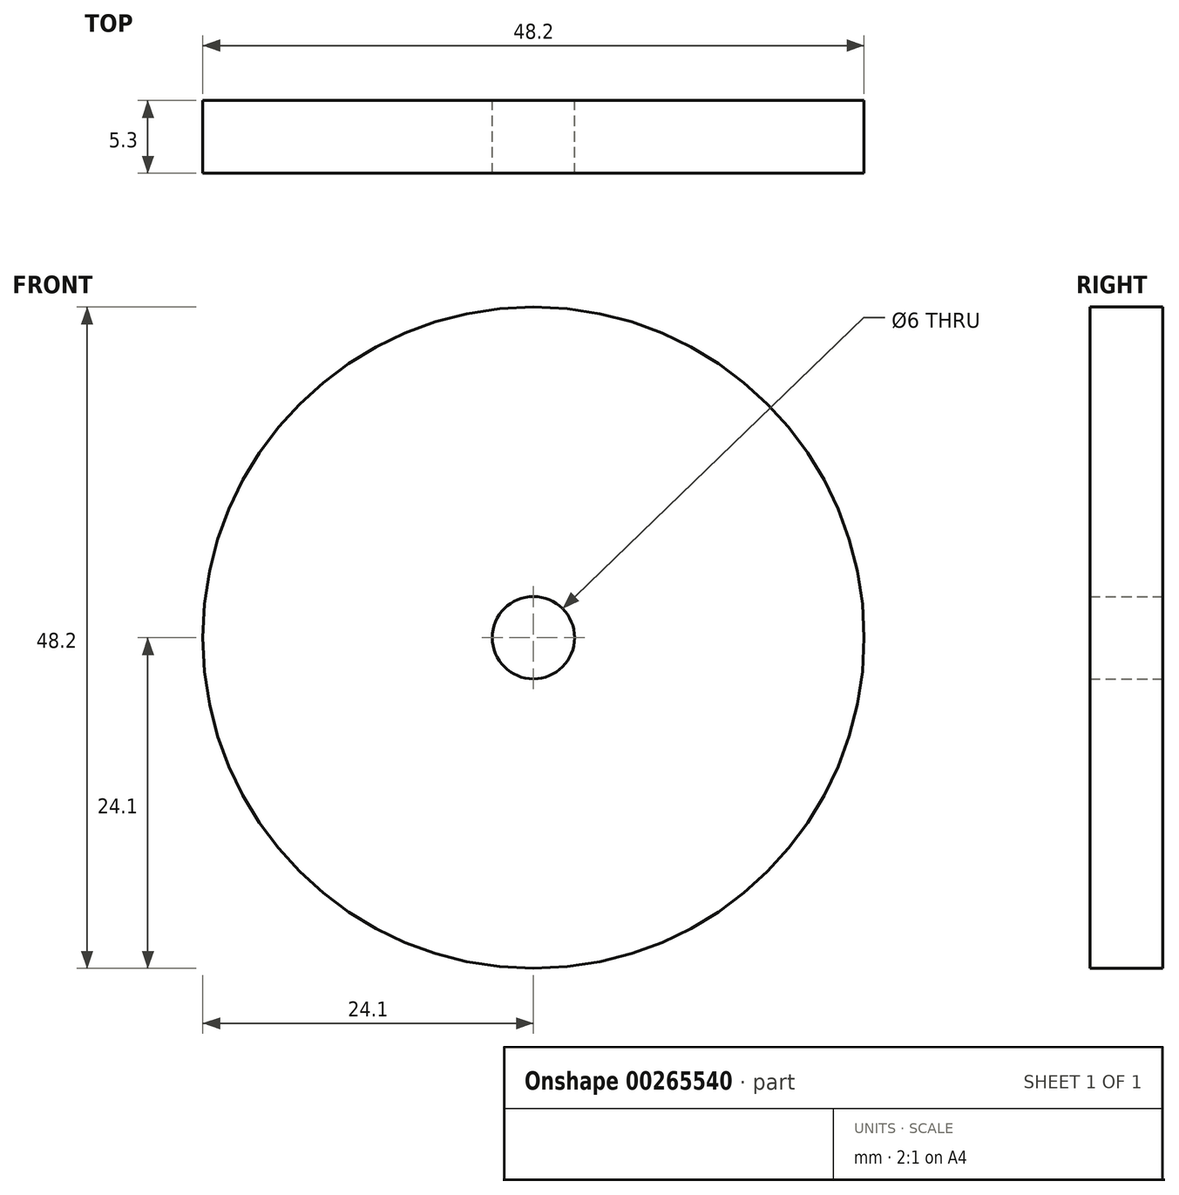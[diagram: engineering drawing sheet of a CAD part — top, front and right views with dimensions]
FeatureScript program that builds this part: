
annotation { "Feature Type Name" : "Feature", "Feature Type Description" : "" }
export const myFeature = defineFeature(function(context is Context, id is Id, definition is map)
    precondition{}
    {
        {
            var Q0;
            Q0=qCreatedBy(makeId("Front.planeOp"),FACE);
            var sketch = newSketch(context, id + "F0", { "sketchPlane" : qUnion([Q0])});
            skCircle(sketch, "E0", {"center": v(0, 0) * mm, "radius": 24.1 * mm});
            skCircle(sketch, "E1", {"center": v(0, 0) * mm, "radius": 3 * mm});
            skSolve(sketch);
        }
        {
            var Q0;
            Q0=makeQuery(id+"F0.imprint","IMPRINT",FACE,{"disambiguationData":[TD([[makeQuery(id+"F0.imprint","IMPRINT",EDGE,{"derivedFrom":sQuery(id+"F0.wireOp",EDGE,"E0")}),1.0]])]});
            extrude(context, id + "F1", {"entities" : qUnion([Q0]), "depth" : 5.3 * mm});
        }
    });
